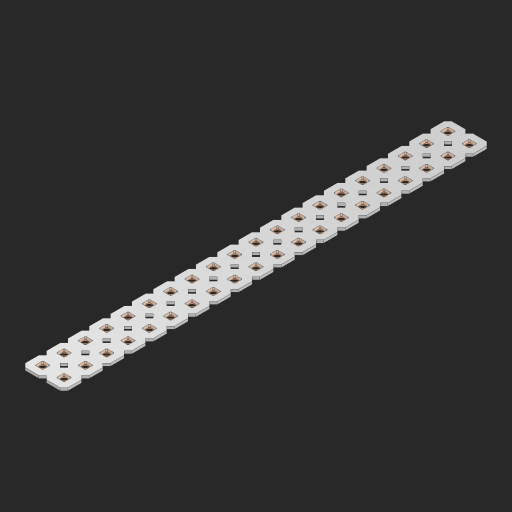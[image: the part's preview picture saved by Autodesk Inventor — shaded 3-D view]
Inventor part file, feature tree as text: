
AUTODESK INVENTOR PART (.ipt)
format: ipt  version: 2023 (Build 270158000, 158)  size: 732,672 bytes
history: native  units: in
note: dims shown in document units (in); Inventor stores cm internally (conversion verified against a paired STEP export)
features: other x41, extrude x39, sketch x2, pattern_linear x1
ambient origin geometry x8: Origin, YZ Plane, XZ Plane, XY Plane, X Axis, Y Axis, Z Axis, Center Point
bodies: Solid1 (feature_tree), Body (feature_tree)
feature tree (83):
  pattern_linear  "Rectangular Pattern1"  Spacing1=0.09in  [1 undecoded]
  sketch  "Sketch1"  dims[d1=0.5in]
  sketch  "Sketch2"  dims[d2=0.182in d3=0.09in d4=0.09in d5=0.09in d6=0.09in d7=0.09in d8=0.09in d9=0.09in d10=0.09in d11=0.02in d13=0.0in d14=0.172in d15=0.0625in d16=0.0in d19=0.5in d22=0.5in]
  other  "Srf1"
  other  "Srf126"
  other  "Srf127"
  other  "Srf128"
  other  "Srf129"
  other  "Srf130"
  other  "Srf131"
  other  "Srf250"
  other  "Srf251"
  other  "Srf252"
  other  "Srf253"
  other  "Srf254"
  other  "Srf255"
  other  "Srf256"
  other  "Srf257"
  other  "Srf258"
  other  "Srf259"
  other  "Srf260"
  other  "Srf261"
  other  "Srf262"
  other  "Srf268"
  other  "Srf269"
  other  "Srf270"
  other  "Srf271"
  other  "Srf272"
  other  "Srf273"
  other  "Srf274"
  other  "Srf275"
  other  "Srf276"
  other  "Srf277"
  other  "Srf278"
  other  "Srf279"
  other  "Srf280"
  other  "Srf281"
  other  "Srf282"
  other  "Srf283"
  other  "Srf284"
  other  "Srf285"
  other  "Srf286"
  other  "Srf287"
  other  "Circle"
  extrude  "ExtrusionSrf126"  Depth=0.09in
  extrude  "ExtrusionSrf127"  Depth=0.09in
  extrude  "ExtrusionSrf128"  Depth=0.09in
  extrude  "ExtrusionSrf129"  Depth=0.09in
  extrude  "ExtrusionSrf130"  Depth=0.09in
  extrude  "ExtrusionSrf131"  Depth=0.09in
  extrude  "ExtrusionSrf250"  Depth=0.09in
  extrude  "ExtrusionSrf251"  Depth=0.02in
  extrude  "ExtrusionSrf252"  TaperAngle=0.0deg  [1 undecoded]
  extrude  "ExtrusionSrf253"  Depth=0.5in
  extrude  "ExtrusionSrf254"  Depth=0.0625in TaperAngle=0.0deg
  extrude  "ExtrusionSrf255"  Depth=0.5in
  extrude  "ExtrusionSrf256"  Depth=0.5in
  extrude  "ExtrusionSrf257"  [1 undecoded]
  extrude  "ExtrusionSrf258"  [1 undecoded]
  extrude  "ExtrusionSrf259"  [1 undecoded]
  extrude  "ExtrusionSrf260"  [1 undecoded]
  extrude  "ExtrusionSrf261"  [1 undecoded]
  extrude  "ExtrusionSrf262"  [1 undecoded]
  extrude  "ExtrusionSrf268"  [1 undecoded]
  extrude  "ExtrusionSrf269"  [1 undecoded]
  extrude  "ExtrusionSrf270"  [1 undecoded]
  extrude  "ExtrusionSrf271"  [1 undecoded]
  extrude  "ExtrusionSrf272"  [1 undecoded]
  extrude  "ExtrusionSrf273"  [1 undecoded]
  extrude  "ExtrusionSrf274"  [1 undecoded]
  extrude  "ExtrusionSrf275"  [1 undecoded]
  extrude  "ExtrusionSrf276"  [1 undecoded]
  extrude  "ExtrusionSrf277"  [1 undecoded]
  extrude  "ExtrusionSrf278"  [1 undecoded]
  extrude  "ExtrusionSrf279"  [1 undecoded]
  extrude  "ExtrusionSrf280"  [1 undecoded]
  extrude  "ExtrusionSrf281"  [1 undecoded]
  extrude  "ExtrusionSrf282"  [1 undecoded]
  extrude  "ExtrusionSrf283"  [1 undecoded]
  extrude  "ExtrusionSrf284"  [1 undecoded]
  extrude  "ExtrusionSrf285"  [1 undecoded]
  extrude  "ExtrusionSrf286"  [1 undecoded]
  extrude  "ExtrusionSrf287"  [1 undecoded]
note: 28 required parameter values undecoded (feature->parameter linkage not recoverable at this tier; creation-order binding heuristic only, values carry confidence <= 0.55)
